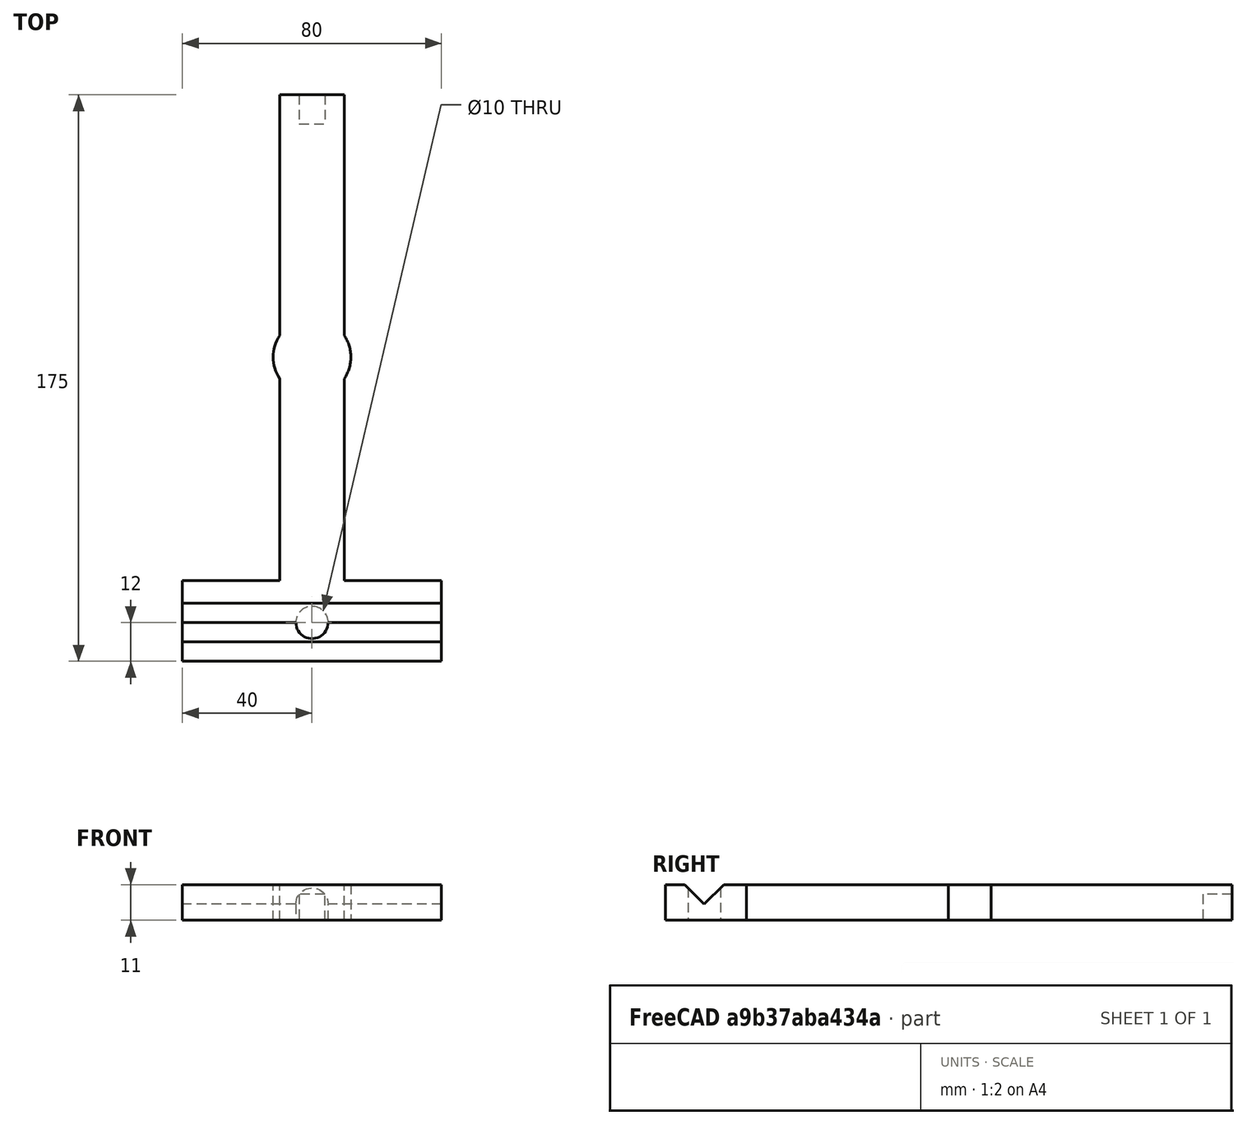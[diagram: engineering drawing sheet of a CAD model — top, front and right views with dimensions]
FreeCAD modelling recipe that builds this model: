
FCSTD DOCUMENT  (FreeCAD 0.19R)
Label: 26erBottom
License: All rights reserved
LicenseURL: http://en.wikipedia.org/wiki/All_rights_reserved
objects: Sketcher::SketchObject×5, PartDesign::Pocket×3, PartDesign::Pad×2, PartDesign::Body×1, Mesh::Feature×1
note: 16 computed .brp shape members not serialized (recipe doc carries the construction recipe); baked Part::Feature solids carry a one-line shape summary decoded from their .brp

FEATURE [Sketcher::SketchObject] Sketch
  FullyConstrained = true
  MapMode = 5
  Support = -> [XY_Plane]
  sketch-geometry (8):
    g0: LineSegment StartX=-40 StartY=-12 StartZ=0 EndX=40 EndY=-12 EndZ=0
    g1: LineSegment StartX=40 StartY=-12 StartZ=0 EndX=40 EndY=13 EndZ=0
    g2: LineSegment StartX=40 StartY=13 StartZ=0 EndX=10 EndY=13 EndZ=0
    g3: LineSegment StartX=10 StartY=13 StartZ=0 EndX=10 EndY=163 EndZ=0
    g4: LineSegment StartX=10 StartY=163 StartZ=0 EndX=-10 EndY=163 EndZ=0
    g5: LineSegment StartX=-10 StartY=163 StartZ=0 EndX=-10 EndY=13 EndZ=0
    g6: LineSegment StartX=-10 StartY=13 StartZ=0 EndX=-40 EndY=13 EndZ=0
    g7: LineSegment StartX=-40 StartY=13 StartZ=0 EndX=-40 EndY=-12 EndZ=0
  constraints (21):
    c: Coincident(g0,g1)
    c: Vertical(g1)
    c: Coincident(g1,g2)
    c: Coincident(g2,g3)
    c: Vertical(g3)
    c: Coincident(g3,g4)
    c: Coincident(g4,g5)
    c: Coincident(g5,g6)
    c: Coincident(g6,g7)
    c: Coincident(g7,g0)
    c: Symmetric(g3,g4,g-2)
    c: Symmetric(g0,g0,g-2)
    c: Equal(g7,g1)
    c: Vertical(g7)
    c: Horizontal(g2)
    c: Symmetric(g2,g5,g-2)
    c: Distance(g4) = 20
    c: Distance(g1) = 25
    c: Distance(g3) = 150
    c: Distance(g0) = 80
    c: DistanceY(g0) = -12
FEATURE [PartDesign::Pad] Pad
  Direction = (1,1,1)
  Length = 11
  Length2 = 100
  Profile = -> Sketch
  Type = 0
FEATURE [Sketcher::SketchObject] Sketch001
  FullyConstrained = true
  MapMode = 5
  Placement = pos=(0,0,11) rot=(0,0,1;0rad)
  Support = -> [Pad]
  sketch-geometry (2):
    g0: Circle CenterX=0 CenterY=82 CenterZ=0 NormalX=0 NormalY=0 NormalZ=1 AngleXU=0 Radius=12
    g1: LineSegment StartX=-25.5 StartY=70 StartZ=0 EndX=25.5 EndY=70 EndZ=0
  constraints (6):
    c: PointOnObject(g0,g-2)
    c: Radius(g0) = 12
    c: Symmetric(g1,g1,g-2)
    c: Distance(g1) = 51
    c: DistanceY(g1) = 70
    c: Tangent(g0,g1)
FEATURE [PartDesign::Pad] Pad001
  BaseFeature = -> Pad
  Direction = (1,1,1)
  Length = 11
  Length2 = 100
  Profile = -> Sketch001
  Reversed = true
  Type = 0
FEATURE [Sketcher::SketchObject] Sketch002
  ExternalGeometry = -> [Pad001]
  FullyConstrained = true
  MapMode = 5
  Placement = pos=(40,0,0) rot=(0.57735,0.57735,0.57735;2.0944rad)
  Support = -> [Pad001]
  sketch-geometry (3):
    g0: LineSegment StartX=16.645 StartY=21.645 StartZ=0 EndX=0 EndY=5 EndZ=0
    g1: LineSegment StartX=0 StartY=5 StartZ=0 EndX=-16.645 EndY=21.645 EndZ=0
    g2: LineSegment StartX=-16.645 StartY=21.645 StartZ=0 EndX=16.645 EndY=21.645 EndZ=0
  constraints (8):
    c: PointOnObject(g0,g-2)
    c: Coincident(g0,g1)
    c: Coincident(g1,g2)
    c: Coincident(g2,g0)
    c: Symmetric(g0,g1,g-2)
    c: Angle(g0,g1) = 1.5708
    c: DistanceY(g0) = 5
    c: Distance(g2) = 33.29
FEATURE [PartDesign::Pocket] Pocket
  BaseFeature = -> Pad001
  Length = 5
  Length2 = 100
  Profile = -> Sketch002
  Type = 1
FEATURE [Sketcher::SketchObject] Sketch003
  FullyConstrained = true
  MapMode = 5
  Placement = pos=(0,163,0) rot=(0,0.707107,0.707107;3.14159rad)
  Support = -> [Pocket]
  sketch-geometry (4):
    g0: LineSegment StartX=-3.95 StartY=8 StartZ=0 EndX=3.95 EndY=8 EndZ=0
    g1: LineSegment StartX=3.95 StartY=8 StartZ=0 EndX=3.95 EndY=0 EndZ=0
    g2: LineSegment StartX=3.95 StartY=0 StartZ=0 EndX=-3.95 EndY=0 EndZ=0
    g3: LineSegment StartX=-3.95 StartY=0 StartZ=0 EndX=-3.95 EndY=8 EndZ=0
  constraints (11):
    c: Coincident(g0,g1)
    c: Coincident(g1,g2)
    c: Coincident(g2,g3)
    c: Coincident(g3,g0)
    c: Horizontal(g0)
    c: Horizontal(g2)
    c: Vertical(g1)
    c: Vertical(g3)
    c: Distance(g0) = 7.9
    c: Distance(g1) = 8
    c: Symmetric(g1,g2,g-1)
FEATURE [PartDesign::Pocket] Pocket001
  BaseFeature = -> Pocket
  Length = 9
  Length2 = 100
  Profile = -> Sketch003
  Type = 0
FEATURE [Sketcher::SketchObject] Sketch004
  FullyConstrained = true
  MapMode = 5
  Placement = pos=(0,0,0) rot=(1,0,0;3.14159rad)
  Support = -> [Pocket001]
  sketch-geometry (1):
    g0: Circle CenterX=0 CenterY=0 CenterZ=0 NormalX=0 NormalY=0 NormalZ=1 AngleXU=0 Radius=5
  constraints (2):
    c: Coincident(g0,g-1)
    c: Radius(g0) = 5
FEATURE [PartDesign::Pocket] Pocket002
  BaseFeature = -> Pocket001
  Length = 5
  Length2 = 100
  Profile = -> Sketch004
  Type = 1
FEATURE [PartDesign::Body] Body
  Group = -> [Sketch,Pad,Sketch001,Pad001,Sketch002,Pocket,Sketch003,Pocket001,Sketch004,Pocket002]
  Origin = -> Origin
  Tip = -> Pocket002
FEATURE [Mesh::Feature] Mesh  label="Pocket002 (Meshed)"
